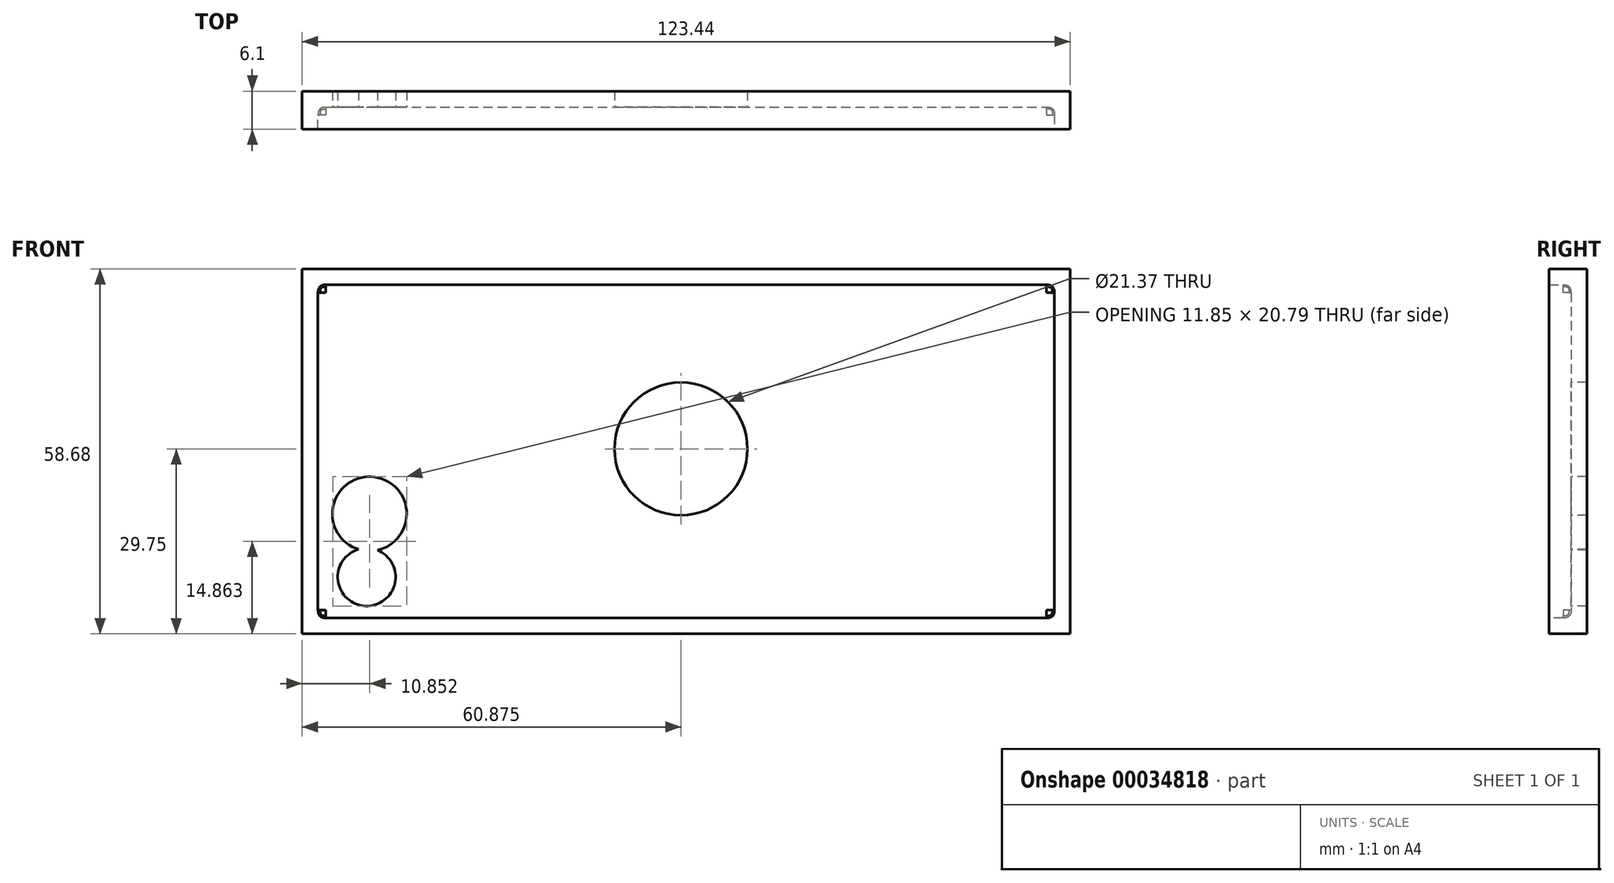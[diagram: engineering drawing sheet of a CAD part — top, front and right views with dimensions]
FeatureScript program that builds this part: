
annotation { "Feature Type Name" : "Feature", "Feature Type Description" : "" }
export const myFeature = defineFeature(function(context is Context, id is Id, definition is map)
    precondition{}
    {
        {
            var Q0;
            Q0=qCreatedBy(makeId("Front.planeOp"),FACE);
            var sketch = newSketch(context, id + "F0", { "sketchPlane" : qUnion([Q0])});
            skLineSegment(sketch, "E0.bottom", {"start": v(74.7, 28.93) * mm, "end": v(-48.74, 28.93) * mm});
            skLineSegment(sketch, "E0.top", {"start": v(74.7, -29.75) * mm, "end": v(-48.74, -29.75) * mm});
            skLineSegment(sketch, "E0.left", {"start": v(74.7, 28.93) * mm, "end": v(74.7, -29.75) * mm});
            skLineSegment(sketch, "E0.right", {"start": v(-48.74, 28.93) * mm, "end": v(-48.74, -29.75) * mm});
            skSolve(sketch);
        }
        {
            var Q0;
            Q0=makeQuery(id+"F0.imprint","IMPRINT",FACE,{"disambiguationData":[TD([[makeQuery(id+"F0.imprint","IMPRINT",EDGE,{"derivedFrom":sQuery(id+"F0.wireOp",EDGE,"E0.bottom")}),1.0]])]});
            extrude(context, id + "F1", {"entities" : qUnion([Q0]), "depth" : 6.1 * mm});
        }
        {
            var Q0;
            Q0=makeQuery(id+"F1.opExtrude","CAP_FACE",FACE,{"disambiguationData":[OSD([sQuery(id+"F0.wireOp",EDGE,"E0.bottom"),sQuery(id+"F0.wireOp",EDGE,"E0.top"),sQuery(id+"F0.wireOp",EDGE,"E0.left"),sQuery(id+"F0.wireOp",EDGE,"E0.right")])],"isStart":false});
            shell(context, id + "F2", {"entities" : qUnion([Q0]), "thickness" : 2.54 * mm});
        }
        {
            var Q0;
            {var subQ0=sQuery(id+"F0.wireOp",EDGE,"E0.top");Q0=makeQuery(id+"F2.opShell","OFFSET_EDGE",EDGE,{"disambiguationData":[OSD([subQ0]),TDD([makeQuery(id+"F1.opExtrude","CAP_EDGE",EDGE,{"disambiguationData":[OSD([subQ0])],"isStart":true})])]});}
            var Q1;
            {var subQ0=sQuery(id+"F0.wireOp",EDGE,"E0.right");Q1=makeQuery(id+"F2.opShell","OFFSET_EDGE",EDGE,{"disambiguationData":[OSD([subQ0]),TDD([makeQuery(id+"F1.opExtrude","CAP_EDGE",EDGE,{"disambiguationData":[OSD([subQ0])],"isStart":true})])]});}
            var Q2;
            {var subQ0=sQuery(id+"F0.wireOp",EDGE,"E0.bottom");Q2=makeQuery(id+"F2.opShell","OFFSET_EDGE",EDGE,{"disambiguationData":[OSD([subQ0]),TDD([makeQuery(id+"F1.opExtrude","CAP_EDGE",EDGE,{"disambiguationData":[OSD([subQ0])],"isStart":true})])]});}
            var Q3;
            {var subQ0=sQuery(id+"F0.wireOp",EDGE,"E0.left");Q3=makeQuery(id+"F2.opShell","OFFSET_EDGE",EDGE,{"disambiguationData":[OSD([subQ0]),TDD([makeQuery(id+"F1.opExtrude","CAP_EDGE",EDGE,{"disambiguationData":[OSD([subQ0])],"isStart":true})])]});}
            var Q4;
            Q4=makeQuery(id+"F2.opShell","OFFSET_EDGE",EDGE,{"disambiguationData":[OSD([sQuery(id+"F0.wireOp",EDGE,"E0.bottom"),sQuery(id+"F0.wireOp",EDGE,"E0.left")])]});
            var Q5;
            Q5=makeQuery(id+"F2.opShell","OFFSET_EDGE",EDGE,{"disambiguationData":[OSD([sQuery(id+"F0.wireOp",EDGE,"E0.top"),sQuery(id+"F0.wireOp",EDGE,"E0.right")])]});
            var Q6;
            Q6=makeQuery(id+"F2.opShell","OFFSET_EDGE",EDGE,{"disambiguationData":[OSD([sQuery(id+"F0.wireOp",EDGE,"E0.top"),sQuery(id+"F0.wireOp",EDGE,"E0.left")])]});
            var Q7;
            Q7=makeQuery(id+"F2.opShell","OFFSET_EDGE",EDGE,{"disambiguationData":[OSD([sQuery(id+"F0.wireOp",EDGE,"E0.bottom"),sQuery(id+"F0.wireOp",EDGE,"E0.right")])]});
            fillet(context, id + "F3", {"entities" : qUnion([Q0, Q1, Q2, Q3, Q4, Q5, Q6, Q7]), "radius" : 1.27 * mm, "tangentPropagation" : true, "rho" : 0.5, "crossSection" : FilletCrossSection.CONIC, "allowEdgeOverflow" : false});
        }
        {
            var Q0;
            Q0=makeQuery(id+"F2.opShell","OFFSET_FACE",FACE,{"disambiguationData":[OSD([sQuery(id+"F0.wireOp",EDGE,"E0.bottom"),sQuery(id+"F0.wireOp",EDGE,"E0.top"),sQuery(id+"F0.wireOp",EDGE,"E0.left"),sQuery(id+"F0.wireOp",EDGE,"E0.right")])]});
            var sketch = newSketch(context, id + "F4", { "sketchPlane" : qUnion([Q0])});
            skCircle(sketch, "E1", {"center": v(-38.38, -20.64) * mm, "radius": 4.65 * mm});
            skCircle(sketch, "E2", {"center": v(12.14, 0) * mm, "radius": 10.68 * mm});
            skSolve(sketch);
        }
        {
            var Q0;
            Q0 = qSketchRegion(id + "F4", true);
            extrude(context, id + "F5", {"entities" : qUnion([Q0]), "operationType" : NewBodyOperationType.REMOVE, "oppositeDirection" : true, "depth" : 25.4 * mm});
        }
        {
            var Q0;
            Q0=makeQuery(id+"F2.opShell","OFFSET_FACE",FACE,{"disambiguationData":[OSD([sQuery(id+"F0.wireOp",EDGE,"E0.bottom"),sQuery(id+"F0.wireOp",EDGE,"E0.top"),sQuery(id+"F0.wireOp",EDGE,"E0.left"),sQuery(id+"F0.wireOp",EDGE,"E0.right")])]});
            var sketch = newSketch(context, id + "F6", { "sketchPlane" : qUnion([Q0])});
            skCircle(sketch, "E3", {"center": v(-37.92, -10.46) * mm, "radius": 5.98 * mm});
            skSolve(sketch);
        }
        {
            var Q0;
            Q0 = qSketchRegion(id + "F6", true);
            extrude(context, id + "F7", {"entities" : qUnion([Q0]), "operationType" : NewBodyOperationType.REMOVE, "oppositeDirection" : true, "depth" : 25.4 * mm});
        }
    });
